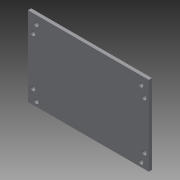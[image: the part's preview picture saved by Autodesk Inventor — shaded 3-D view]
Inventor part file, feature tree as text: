
AUTODESK INVENTOR PART (.ipt)
format: ipt  version: 2013 (Build 170138000, 138)  size: 108,544 bytes
history: native  units: mm
features: sketch x3, extrude x2, other x1, hole x1
ambient origin geometry x8: Origin, YZ Plane, XZ Plane, XY Plane, X Axis, Y Axis, Z Axis, Center Point
feature tree (7):
  other  "ソリッド1"
  extrude  "押し出し1"  Depth=76.0mm
  extrude  "押し出し2"  Depth=50.0mm
  hole  "穴1"  [1 undecoded]
  sketch  "スケッチ1"
  sketch  "スケッチ2"
  sketch  "スケッチ3"
note: 1 required parameter value undecoded (feature->parameter linkage not recoverable at this tier; creation-order binding heuristic only, values carry confidence <= 0.55)
